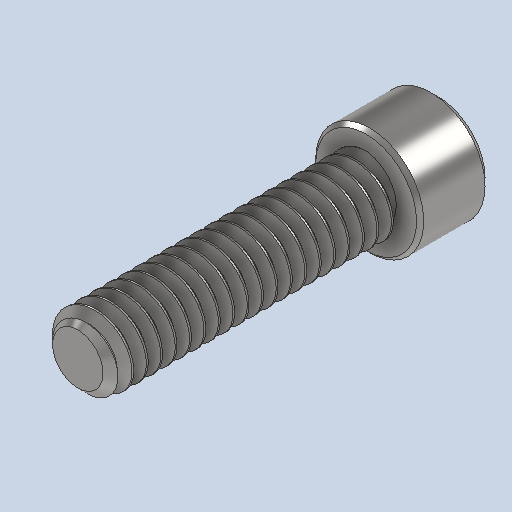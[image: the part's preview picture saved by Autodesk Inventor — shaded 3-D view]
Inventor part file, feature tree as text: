
AUTODESK INVENTOR PART (.ipt)
format: ipt  version: 2024 (Build 280153000, 153)  size: 769,024 bytes
history: native  units: in
note: dims shown in document units (in); Inventor stores cm internally (conversion verified against a paired STEP export)
features: chamfer x1
ambient origin geometry x8: Origin, YZ Plane, XZ Plane, XY Plane, X Axis, Y Axis, Z Axis, Center Point
bodies: Solid1 (feature_tree)
feature tree (1):
  chamfer  "Chamfer2"  [1 undecoded]
note: 1 required parameter value undecoded (feature->parameter linkage not recoverable at this tier; creation-order binding heuristic only, values carry confidence <= 0.55)
